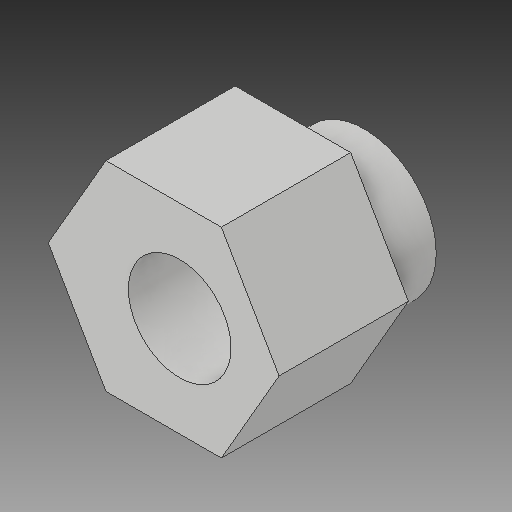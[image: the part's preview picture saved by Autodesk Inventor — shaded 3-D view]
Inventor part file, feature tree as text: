
AUTODESK INVENTOR PART (.ipt)
format: ipt  version: 2018 (Build 220112000, 112)  size: 113,152 bytes
history: native  units: mm
features: other x3, sketch x3
ambient origin geometry x8: Origin, YZ Plane, XZ Plane, XY Plane, X Axis, Y Axis, Z Axis, Center Point
bodies: Solid1 (feature_tree)
feature tree (6):
  other  "Eccentric Spacer.ipt"
  other  "Solid1::Eccentric Spacer.ipt"
  other  "TaggingFeature1"
  sketch  "Sketch1"  dims[d0=10.0mm]
  sketch  "Sketch2"
  sketch  "Sketch3"
